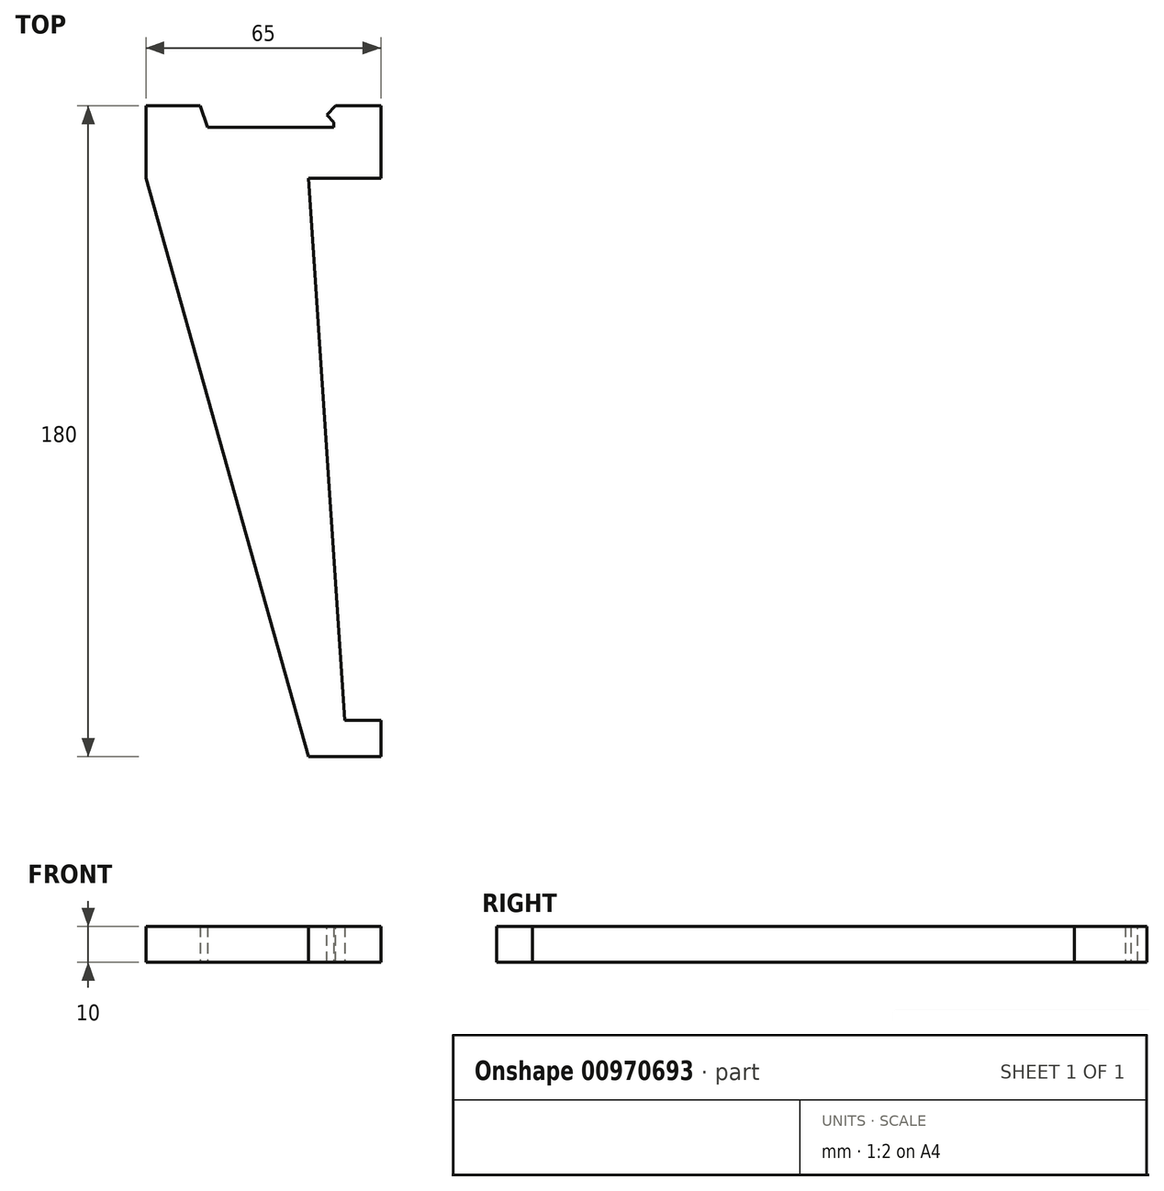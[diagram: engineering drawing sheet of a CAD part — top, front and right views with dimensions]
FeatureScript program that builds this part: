
annotation { "Feature Type Name" : "Feature", "Feature Type Description" : "" }
export const myFeature = defineFeature(function(context is Context, id is Id, definition is map)
    precondition{}
    {
        {
            var Q0;
            Q0=qCreatedBy(makeId("Top.planeOp"),FACE);
            var sketch = newSketch(context, id + "F0", { "sketchPlane" : qUnion([Q0])});
            skLineSegment(sketch, "E0", {"start": v(0, 0) * mm, "end": v(35, 0) * mm});
            skLineSegment(sketch, "E1", {"start": v(35, 0) * mm, "end": v(35, 1.5) * mm});
            skLineSegment(sketch, "E2", {"start": v(35, 1.5) * mm, "end": v(33, 1.5) * mm});
            skLineSegment(sketch, "E3", {"start": v(33, 1.5) * mm, "end": v(33, 6) * mm});
            skLineSegment(sketch, "E4", {"start": v(33, 6) * mm, "end": v(48, 6) * mm});
            skLineSegment(sketch, "E5", {"start": v(48, 6) * mm, "end": v(48, -14) * mm});
            skLineSegment(sketch, "E6", {"start": v(48, -14) * mm, "end": v(-17, -14) * mm});
            skLineSegment(sketch, "E7", {"start": v(-17, -14) * mm, "end": v(-17, 6) * mm});
            skLineSegment(sketch, "E8", {"start": v(-17, 6) * mm, "end": v(-2, 6) * mm});
            skLineSegment(sketch, "E9", {"start": v(-2, 6) * mm, "end": v(0, 0) * mm});
            skPoint(sketch, "E10", {"position": v(28, -14) * mm});
            skLineSegment(sketch, "E11", {"start": v(48, -164) * mm, "end": v(38, -164) * mm});
            skLineSegment(sketch, "E12", {"start": v(38, -164) * mm, "end": v(28, -14) * mm});
            skLineSegment(sketch, "E13", {"start": v(48, -164) * mm, "end": v(48, -174) * mm});
            skLineSegment(sketch, "E14", {"start": v(48, -174) * mm, "end": v(28, -174) * mm});
            skLineSegment(sketch, "E15", {"start": v(28, -174) * mm, "end": v(-17, -14) * mm});
            skSolve(sketch);
        }
        {
            var Q0;
            Q0=makeQuery(id+"F0.imprint","IMPRINT",FACE,{"disambiguationData":[TD([[makeQuery(id+"F0.imprint","IMPRINT",EDGE,{"derivedFrom":sQuery(id+"F0.wireOp",EDGE,"E0")}),-1.0]])]});
            var Q1;
            Q1=makeQuery(id+"F0.imprint","IMPRINT",FACE,{"disambiguationData":[TD([[makeQuery(id+"F0.imprint","IMPRINT",EDGE,{"derivedFrom":sQuery(id+"F0.wireOp",EDGE,"E11")}),1.0]])]});
            extrude(context, id + "F1", {"entities" : qUnion([Q0, Q1]), "depth" : 10 * mm, "offsetDistance" : 25 * mm});
        }
        {
            var Q0;
            Q0=makeQuery(id+"F1.opExtrude","SWEPT_EDGE",EDGE,{"disambiguationData":[OSD([sQuery(id+"F0.wireOp",EDGE,"E2"),sQuery(id+"F0.wireOp",EDGE,"E3")])]});
            chamfer(context, id + "F2", {"entities" : qUnion([Q0]), "width" : 2 * mm, "tangentPropagation" : true});
        }
        {
            var Q0;
            Q0=makeQuery(id+"F1.opExtrude","SWEPT_EDGE",EDGE,{"disambiguationData":[OSD([sQuery(id+"F0.wireOp",EDGE,"E3"),sQuery(id+"F0.wireOp",EDGE,"E4")])]});
            chamfer(context, id + "F3", {"entities" : qUnion([Q0]), "width" : 2.5 * mm, "tangentPropagation" : true});
        }
    });
